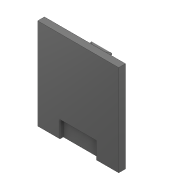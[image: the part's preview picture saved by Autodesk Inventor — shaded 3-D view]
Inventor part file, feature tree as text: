
AUTODESK INVENTOR PART (.ipt)
format: ipt  version: 2020 (Build 240168000, 168)  size: 137,216 bytes
history: native  units: mm
features: extrude x4, sketch x4, fillet x1
ambient origin geometry x8: Origin, YZ Plane, XZ Plane, XY Plane, X Axis, Y Axis, Z Axis, Center Point
bodies: Volumenkörper1 (feature_tree)
feature tree (9):
  extrude  "Extrusion1"  Depth=120.0mm
  extrude  "Extrusion2"  Depth=54.0mm
  extrude  "Extrusion3"  Depth=33.0mm
  extrude  "Extrusion4"  Depth=2.5mm
  fillet  "Rundung1"  Radius=45.0mm
  sketch  "Skizze1"  dims[d0=135.0mm d1=120.0mm]
  sketch  "Skizze2"  dims[d2=10.0mm d3=0.0mm d4=54.0mm]
  sketch  "Skizze3"  dims[d5=25.0mm d6=33.0mm]
  sketch  "Skizze4"  dims[d7=5.0mm d8=0.0mm d9=5.0mm d10=5.0mm d11=5.0mm d12=5.0mm d13=20.0mm d14=20.0mm d15=45.0mm d16=45.0mm d17=20.0mm d18=20.0mm d19=0.0mm d20=5.0mm d21=5.0mm d22=30.0mm d23=0.0mm d24=2.5mm]
